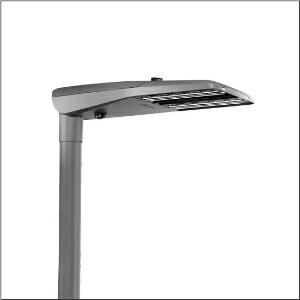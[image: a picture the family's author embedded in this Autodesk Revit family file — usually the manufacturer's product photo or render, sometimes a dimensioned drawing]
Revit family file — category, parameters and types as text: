
# Revit family: streetlight_sl_11_iq_midi___st1_0p1_0_5xc3k51y08me_73ea
name_source: partatom
category: Lighting Fixtures
units: mm (PartAtom-declared; Revit-internal decimal feet)

## family parameters
Cut with Voids When Loaded = No
Host = Face
Light Source = No
Part Type = Normal
Room Calculation Point = No
Round Connector Dimension = Use Diameter
Shared = No

## types (1)
- --- (1 x LED, 17540 lm, 122.7 W, 3000K)
    Apparent Load = 123 VA
    CIE Flux Codes = 32 65 95 100 100
    Color Rendering = 70
    Color Temperature = 3000K
    Default Elevation = 1800 mm
    Description = Streetlight SL 11 iQ midi, mast luminaire, primary light control with 3 zone facetted reflector, of plastic, silver coated, highly specular, primary optical cover: cover, of PMMA, transparent, light distribution: ST1.0P1.0, light emission: direct distribution, primary light characteristic: asymmetric, installation type: post-top, side-entry, LED, High Power LED, rated luminous flux: 17.540lm, luminous efficacy: 143lm/W, light colour: 730, colour temperature: 3000K, control: presetting dimming logarithmic, Street-Remote, Auto-Match, Temp-Guard, Lumen-Switch, Night-Set, Smart-Wire, Light-Fading, Desk-Remote (wireless, voltage-free reading and setting of iQ features in the workshop via application-optimized NFC function/RFID function), optimised constant luminous flux control (CLO 2.0), with cable H07RN-F 5x 1.5mm², mains connection: 230..240V, AC, 50/60Hz, connection cable pre-assembled, cable length: 12,5m, start of lifetime: 123W, end of service life: 130W, reduction: 56W, luminaire housing, of diecast aluminium, powder-coated, Siteco® metallic grey (DB 702S), please order mast flange separately, inclination adjustable without tools: 0°, 5°, 10°, 15° (post-top) | 0°, -5°, -10°, -15° (side-entry), sealing non-destructively replaceable, multi-level sealing system, length: 780mm, width: 376mm, height: 118mm, mast flange for spigot size: 42mm (side-entry): 5XC10008XM4, 60/48mm (side-entry/post-top): 5XC10108XM2, 76/60mm (side-entry/post-top): 5XC10108XM1, equipment: Power, Smart Interface below and above, protection rating (complete): IP66, insulation class (complete): insulation class II (safety insulation), certification: CE, ENEC, VDE, UKCA, impact resistance: IK09, permissible operating ambient temperature for outdoor applications: -25..+50°C, standard-compliant lighting for roads and squares, Environmental Product Declaration (EPD) tested and certified by an independent institute, packaging unit: 1 piece

Light Distribution: ST1.0P1.0
    Height = 118 mm
    Lamp = 1 x LED
    Lamp Light Flux = 17540 lm
    Lamp Power = 122.7 W
    Lamp count = 1
    Length = 780 mm
    Luminous efficacy = 143 lm/W
    Manufacturer = Siteco
    ModVariant = No
    Model = 5XC3K51Y08ME
    Number of Poles = 1
    OnlyDefault = Yes
    Power Factor = 1
    Product Name = Streetlight SL 11 iQ midi | ST1.0P1.0
    Product group = mast luminaire | pylon top
    ProductGroupID = 6100
    Protection Class = Protection class II
    Protection Degree = IP 66
    RLX_Detail_Level = 1
    RLX_Emergency_Light_Flux = 0 lm
    RLX_Emergency_Type = 0
    RLX_Emergency_Type_DB = No
    RlxData = <blob elided: 69657 chars, md5=53322c7f>
    Socket = socket
    Standby Power = 0 W
    System Light Flux = 17540 lm
    System Power = 123 W
    Type Comments = factory setting: luminous flux: 100 % | dim-lin: 254 | 553 mA
    Type Image = l_1004429.jpg
    URL = http://relux.com
    VarID = @adj_003257
    Voltage = 0 V
    Weight = 0.00 kg
    Width = 376 mm

## geometry (parser evidence)
native form markers: Blend x4, Sweep x10
no freeform markers — native parametric forms only
